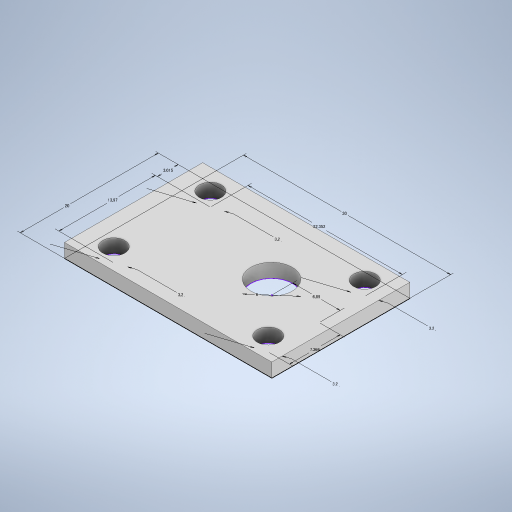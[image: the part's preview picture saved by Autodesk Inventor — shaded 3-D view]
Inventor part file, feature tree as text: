
AUTODESK INVENTOR PART (.ipt)
format: ipt  version: 2024.2 (Build 282272000, 272)  size: 268,288 bytes
history: native  units: mm
features: extrude x2, other x1, sketch x1
ambient origin geometry x8: Origin, YZ Plane, XZ Plane, XY Plane, X Axis, Y Axis, Z Axis, Center Point
bodies: Body1 (feature_tree)
feature tree (4):
  other  "ソリッド1"
  sketch  "スケッチ1"
  extrude  "押し出し1"  Depth=30.0mm
  extrude  "押し出し2"  Depth=20.0mm
